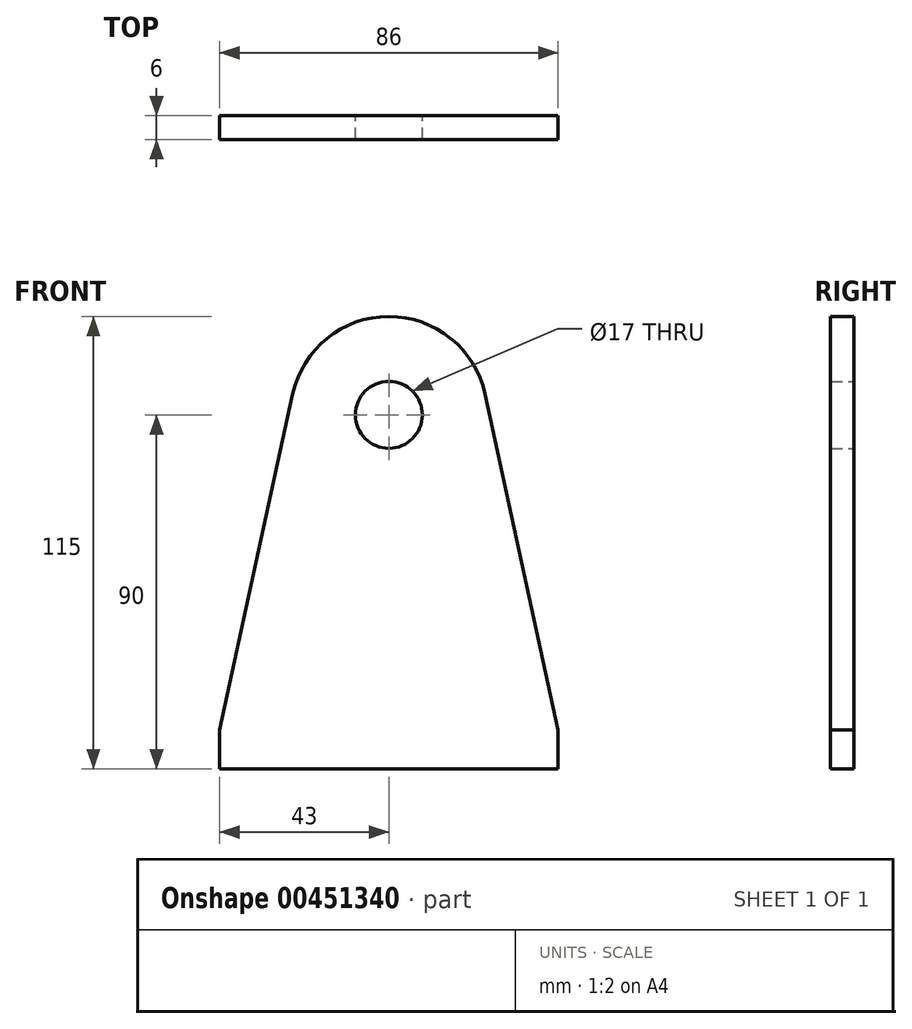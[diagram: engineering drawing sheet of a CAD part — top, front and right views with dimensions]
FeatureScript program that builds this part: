
annotation { "Feature Type Name" : "Feature", "Feature Type Description" : "" }
export const myFeature = defineFeature(function(context is Context, id is Id, definition is map)
    precondition{}
    {
        {
            var Q0;
            Q0=qCreatedBy(makeId("Front.planeOp"),FACE);
            var sketch = newSketch(context, id + "F0", { "sketchPlane" : qUnion([Q0])});
            skLineSegment(sketch, "E0", {"start": v(0, 0) * mm, "end": v(-43, 0) * mm});
            skLineSegment(sketch, "E1", {"start": v(-43, 0) * mm, "end": v(-43, 10) * mm});
            skLineSegment(sketch, "E2", {"start": v(0, 115) * mm, "end": v(0, 98.5) * mm});
            skArc(sketch, "E3", {"start": v(0, 115) * mm, "mid": v(-15.69, 109.47) * mm, "end": v(-24.43, 95.32) * mm});
            skLineSegment(sketch, "E4", {"start": v(-43, 10) * mm, "end": v(-24.43, 95.32) * mm});
            skArc(sketch, "E5", {"start": v(0, 98.5) * mm, "mid": v(-8.5, 90) * mm, "end": v(0, 81.5) * mm});
            skLineSegment(sketch, "E6.trimOffspring", {"start": v(0, 81.5) * mm, "end": v(0, 0) * mm});
            skSolve(sketch);
        }
        {
            var Q0;
            Q0=makeQuery(id+"F0.imprint","IMPRINT",FACE,{"disambiguationData":[TD([[makeQuery(id+"F0.imprint","IMPRINT",EDGE,{"derivedFrom":sQuery(id+"F0.wireOp",EDGE,"E0")}),-1.0]])]});
            extrude(context, id + "F1", {"entities" : qUnion([Q0]), "depth" : 6 * mm});
        }
        {
            var Q0;
            Q0=makeQuery(id+"F1.opExtrude","SWEPT_BODY",BODY,{"disambiguationData":[OSD([sQuery(id+"F0.wireOp",EDGE,"E0"),sQuery(id+"F0.wireOp",EDGE,"E1"),sQuery(id+"F0.wireOp",EDGE,"E2"),sQuery(id+"F0.wireOp",EDGE,"E3"),sQuery(id+"F0.wireOp",EDGE,"E4"),sQuery(id+"F0.wireOp",EDGE,"E5"),sQuery(id+"F0.wireOp",EDGE,"E6.trimOffspring")])]});
            var Q1;
            Q1=qCreatedBy(makeId("Right.planeOp"),FACE);
            mirror(context, id + "F2", {"operationType" : NewBodyOperationType.ADD, "entities" : qUnion([Q0]), "mirrorPlane" : qUnion([Q1])});
        }
    });
